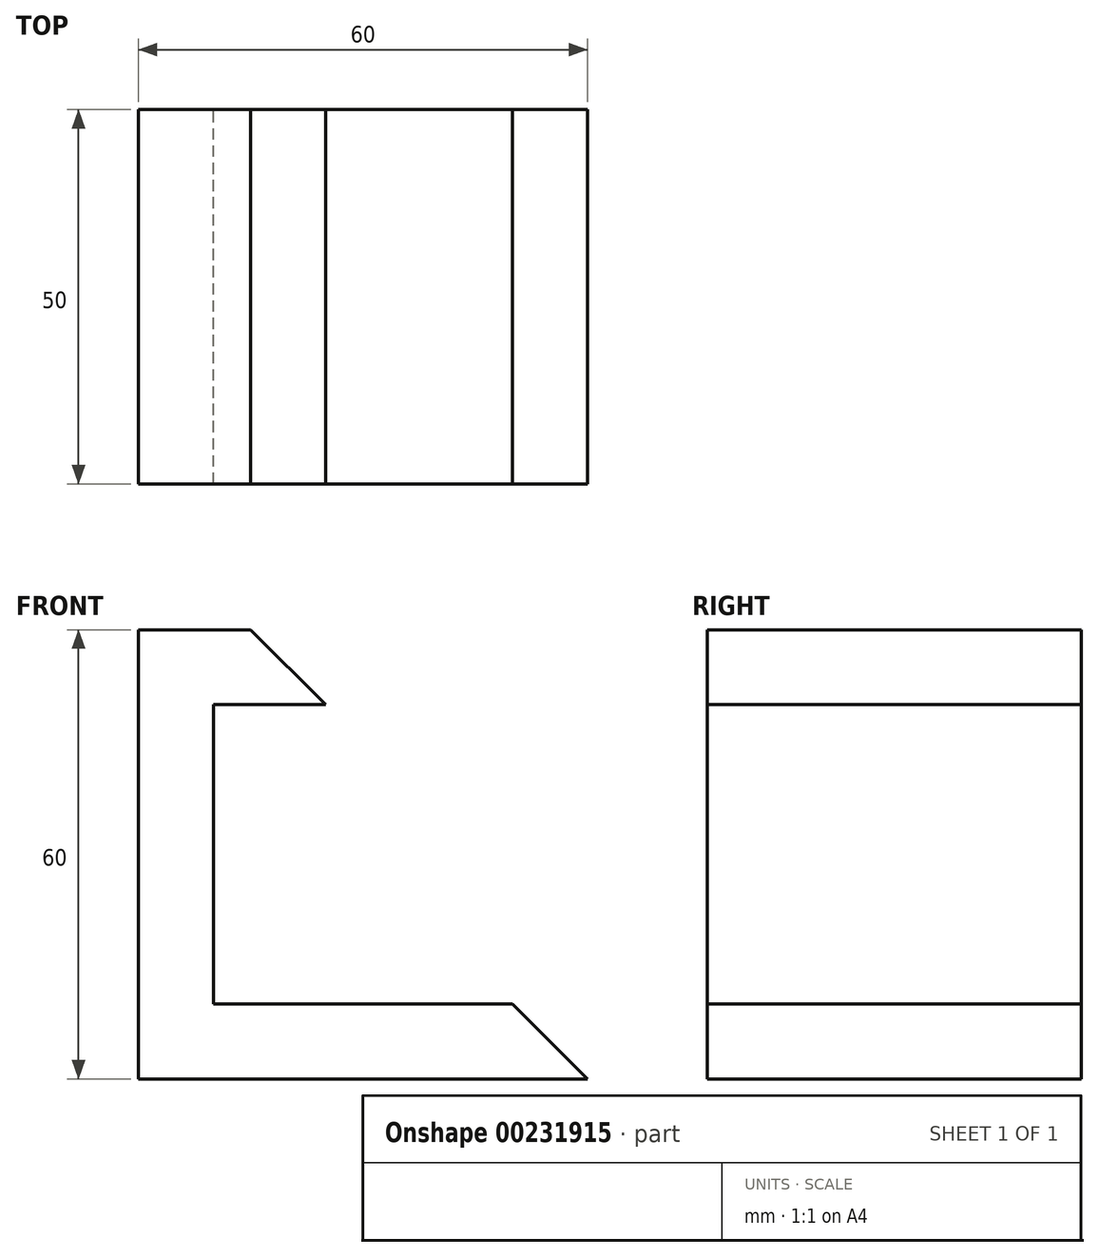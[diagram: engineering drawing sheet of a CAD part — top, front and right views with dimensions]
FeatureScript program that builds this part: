
annotation { "Feature Type Name" : "Feature", "Feature Type Description" : "" }
export const myFeature = defineFeature(function(context is Context, id is Id, definition is map)
    precondition{}
    {
        {
            var Q0;
            Q0=qCreatedBy(makeId("Front.planeOp"),FACE);
            var sketch = newSketch(context, id + "F0", { "sketchPlane" : qUnion([Q0])});
            skLineSegment(sketch, "E0", {"start": v(0, 0) * mm, "end": v(0, 60) * mm});
            skLineSegment(sketch, "E1", {"start": v(0, 60) * mm, "end": v(15, 60) * mm});
            skLineSegment(sketch, "E2", {"start": v(15, 60) * mm, "end": v(25, 50) * mm});
            skLineSegment(sketch, "E3", {"start": v(25, 50) * mm, "end": v(10, 50) * mm});
            skLineSegment(sketch, "E4", {"start": v(10, 50) * mm, "end": v(10, 10) * mm});
            skLineSegment(sketch, "E5", {"start": v(10, 10) * mm, "end": v(50, 10) * mm});
            skLineSegment(sketch, "E6", {"start": v(50, 10) * mm, "end": v(60, 0) * mm});
            skLineSegment(sketch, "E7", {"start": v(60, 0) * mm, "end": v(0, 0) * mm});
            skSolve(sketch);
        }
        {
            var Q0;
            Q0=makeQuery(id+"F0.imprint","IMPRINT",FACE,{"disambiguationData":[TD([[makeQuery(id+"F0.imprint","IMPRINT",EDGE,{"derivedFrom":sQuery(id+"F0.wireOp",EDGE,"E0")}),-1.0]])]});
            extrude(context, id + "F1", {"entities" : qUnion([Q0]), "endBound" : BoundingType.SYMMETRIC, "depth" : 50 * mm});
        }
    });
